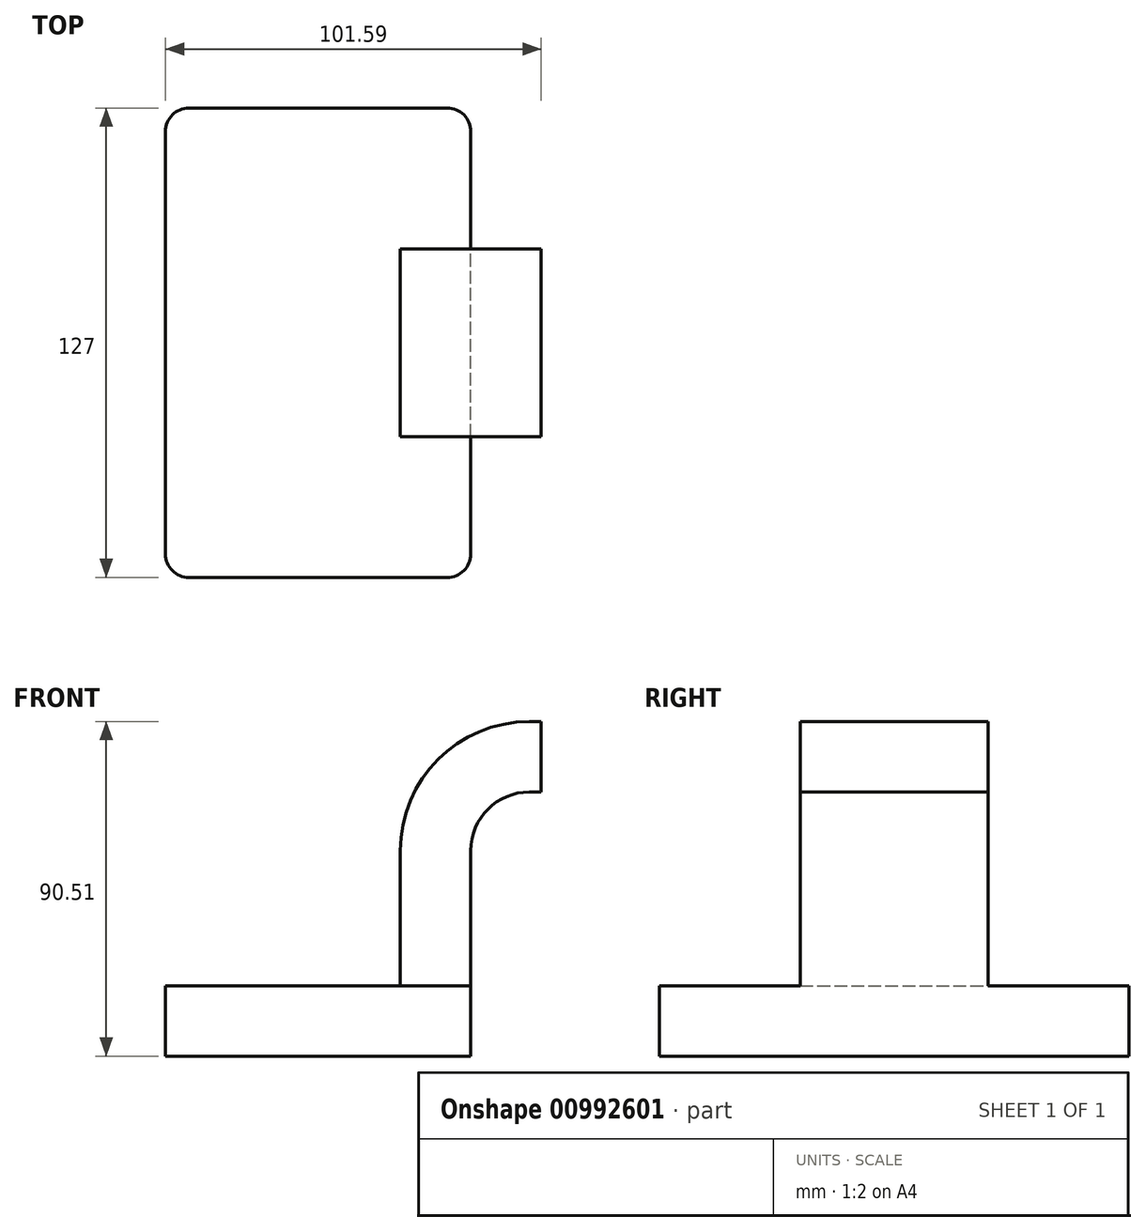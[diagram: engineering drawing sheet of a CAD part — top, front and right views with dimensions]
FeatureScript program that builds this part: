
annotation { "Feature Type Name" : "Feature", "Feature Type Description" : "" }
export const myFeature = defineFeature(function(context is Context, id is Id, definition is map)
    precondition{}
    {
        {
            var Q0;
            Q0=qCreatedBy(makeId("Front.planeOp"),FACE);
            var sketch = newSketch(context, id + "F0", { "sketchPlane" : qUnion([Q0])});
            skLineSegment(sketch, "E0.bottom", {"start": v(-41.28, 9.52) * mm, "end": v(41.28, 9.52) * mm});
            skLineSegment(sketch, "E0.top", {"start": v(-41.28, -9.53) * mm, "end": v(41.28, -9.53) * mm});
            skLineSegment(sketch, "E0.left", {"start": v(-41.28, 9.52) * mm, "end": v(-41.28, -9.53) * mm});
            skLineSegment(sketch, "E0.right", {"start": v(41.28, 9.52) * mm, "end": v(41.28, -9.52) * mm});
            skPoint(sketch, "E0.middle", {"position": v(0, 0) * mm});
            skLineSegment(sketch, "E1", {"start": v(41.27, 9.52) * mm, "end": v(41.27, 46.05) * mm});
            skArc(sketch, "E2", {"start": v(41.27, 46.05) * mm, "mid": v(45.92, 57.28) * mm, "end": v(57.15, 61.93) * mm});
            skLineSegment(sketch, "E3.bottom", {"start": v(60.32, 85.72) * mm, "end": v(111.12, 85.72) * mm});
            skLineSegment(sketch, "E3.top", {"start": v(60.32, 57.15) * mm, "end": v(111.12, 57.15) * mm});
            skLineSegment(sketch, "E3.left", {"start": v(60.32, 85.73) * mm, "end": v(60.32, 57.15) * mm});
            skLineSegment(sketch, "E3.right", {"start": v(111.12, 85.73) * mm, "end": v(111.12, 57.15) * mm});
            skPoint(sketch, "E3.middle", {"position": v(85.72, 71.44) * mm});
            skLineSegment(sketch, "E4", {"start": v(57.15, 61.93) * mm, "end": v(96.98, 61.93) * mm});
            skLineSegment(sketch, "E5.0", {"start": v(57.15, 80.98) * mm, "end": v(96.98, 80.98) * mm});
            skArc(sketch, "E5.1", {"start": v(22.22, 46.05) * mm, "mid": v(32.45, 70.75) * mm, "end": v(57.15, 80.98) * mm});
            skLineSegment(sketch, "E5.2", {"start": v(22.22, 9.52) * mm, "end": v(22.22, 46.05) * mm});
            skLineSegment(sketch, "E6", {"start": v(96.98, 61.93) * mm, "end": v(96.98, 80.98) * mm});
            skFitSpline(sketch, "E7", {"points": [v(-41.28, 9.52) * mm, v(57.15, 80.98) * mm], "startDerivative": vector(38.46, 97.15) * mm, "endDerivative": vector(123.93, -4.82) * mm});
            skLineSegment(sketch, "E8", {"start": v(85.72, 57.15) * mm, "end": v(85.72, 85.72) * mm});
            skSolve(sketch);
        }
        {
            var Q0;
            Q0=makeQuery(id+"F0.imprint","IMPRINT",FACE,{"disambiguationData":[TD([[makeQuery(id+"F0.imprint","IMPRINT",EDGE,{"derivedFrom":sQuery(id+"F0.wireOp",EDGE,"E0.top")}),1.0]])]});
            extrude(context, id + "F1", {"entities" : qUnion([Q0]), "endBound" : BoundingType.SYMMETRIC, "depth" : 127 * mm, "offsetDistance" : 25.4 * mm});
        }
        {
            var Q0;
            {var subQ5=sQuery(id+"F0.wireOp",EDGE,"E1");Q0=makeQuery(id+"F0.imprint","IMPRINT",FACE,{"disambiguationData":[TD([[makeQuery(id+"F0.imprint","IMPRINT",EDGE,{"derivedFrom":subQ5}),1.0]])]});}
            extrude(context, id + "F2", {"entities" : qUnion([Q0]), "operationType" : NewBodyOperationType.ADD, "endBound" : BoundingType.SYMMETRIC, "depth" : 50.8 * mm, "offsetDistance" : 25.4 * mm});
        }
        {
            var Q0;
            Q0=makeQuery(id+"F0.imprint","IMPRINT",FACE,{"disambiguationData":[TD([[makeQuery(id+"F0.imprint","IMPRINT",EDGE,{"derivedFrom":sQuery(id+"F0.wireOp",EDGE,"E5.1")}),1.0]])]});
            extrude(context, id + "F3", {"entities" : qUnion([Q0]), "operationType" : NewBodyOperationType.ADD, "endBound" : BoundingType.SYMMETRIC, "depth" : 15.88 * mm, "offsetDistance" : 25.4 * mm});
        }
        {
            var Q0;
            Q0=sQuery(id+"F0.wireOp",EDGE,"E3.right");
            var Q1;
            Q1=sQuery(id+"F0.wireOp",EDGE,"E8");
            revolve(context, id + "F4", {"bodyType" : ToolBodyType.SURFACE, "surfaceOperationType" : NewSurfaceOperationType.NEW, "surfaceEntities" : qUnion([Q0]), "axis" : qUnion([Q1]), "revolveType" : RevolveType.FULL});
        }
        {
            var Q0;
            Q0=makeQuery(id+"F1.opExtrude","CAP_EDGE",EDGE,{"disambiguationData":[OSD([sQuery(id+"F0.wireOp",EDGE,"E0.left")])],"isStart":false});
            var Q1;
            Q1=makeQuery(id+"F1.opExtrude","CAP_EDGE",EDGE,{"disambiguationData":[OSD([sQuery(id+"F0.wireOp",EDGE,"E0.right")])],"isStart":false});
            var Q2;
            Q2=makeQuery(id+"F1.opExtrude","CAP_EDGE",EDGE,{"disambiguationData":[OSD([sQuery(id+"F0.wireOp",EDGE,"E0.right")])],"isStart":true});
            var Q3;
            Q3=makeQuery(id+"F1.opExtrude","CAP_EDGE",EDGE,{"disambiguationData":[OSD([sQuery(id+"F0.wireOp",EDGE,"E0.left")])],"isStart":true});
            fillet(context, id + "F5", {"entities" : qUnion([Q0, Q1, Q2, Q3]), "radius" : 6.35 * mm, "tangentPropagation" : true, "allowEdgeOverflow" : false});
        }
    });
